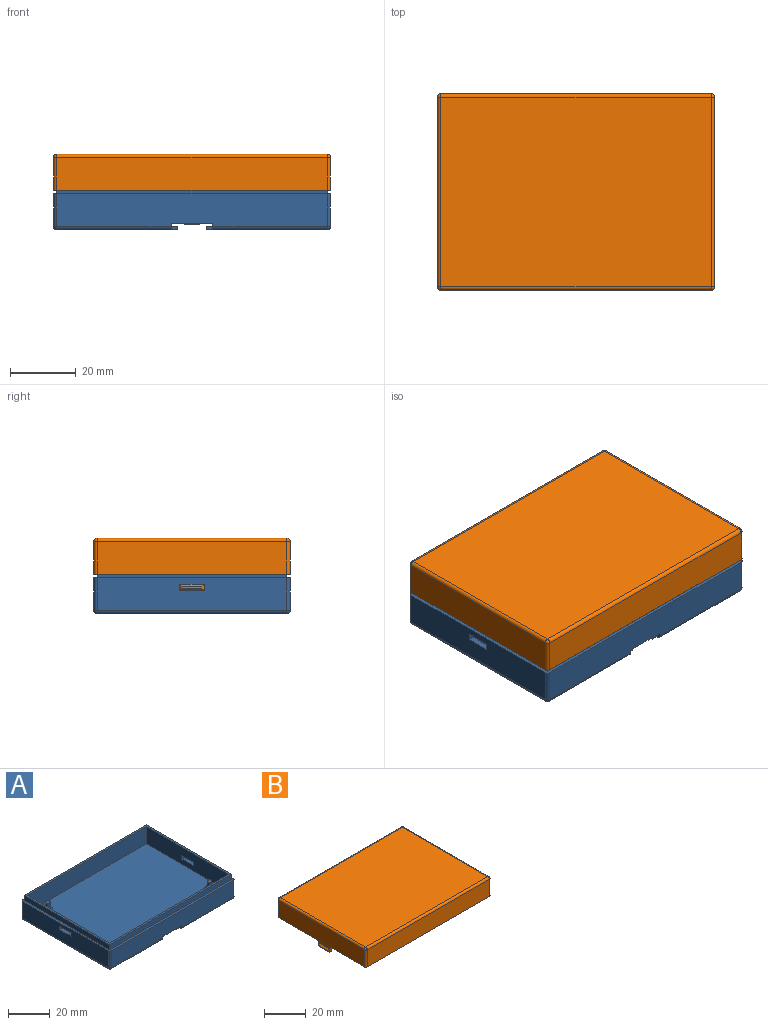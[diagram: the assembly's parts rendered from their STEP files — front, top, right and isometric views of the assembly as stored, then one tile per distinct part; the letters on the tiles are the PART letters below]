
ASSEMBLY  parts=2 mates=1
PART A: 106 faces, bbox 84.3x59.8x14 mm
  f0: plane 82.25x10mm, normal (0,-1,0), area 809.8mm2, adj f30,f32,f45,f69,f88,f90,f95,f97
  f1: plane 82.25x10mm, normal (0,1,0), area 809.8mm2, adj f30,f43,f55,f69,f84,f85,f91,f92
  f2: plane 57.75x10mm, normal (1,0,0), area 562.5mm2, adj f69,f80,f81,f82,f83,f91,f94,f97
  f3: plane 57.75x10mm, normal (-1,0,0), area 562.5mm2, adj f69,f76,f77,f78,f79,f85,f87,f88
  f4: plane 57.75x36.75mm, normal (0,0,-1), area 2104.3mm2, adj f6,f7,f8,f9,f44,f45,f46,f47
  f5: plane 57.75x36.75mm, normal (0,0,-1), area 2104.3mm2, adj f26,f27,f28,f29,f31,f32,f33,f34
  f6: plane 12.19x1mm, normal (-1,0,0), area 12.2mm2, adj f4,f10,f53,f56
  f7: plane 12.19x1mm, normal (-1,0,0), area 12.2mm2, adj f4,f11,f50,f52
  f8: plane 12.19x1mm, normal (-1,0,0), area 12.2mm2, adj f4,f12,f46,f49
  f9: plane 12.19x1mm, normal (-1,0,0), area 12.2mm2, adj f4,f13,f44,f47
  f10: plane 12.19x1.88mm, normal (0,0,1), area 22.9mm2, adj f6,f14,f53,f56
  f11: plane 12.19x1.88mm, normal (0,0,1), area 22.9mm2, adj f7,f15,f50,f52
  f12: plane 12.19x1.88mm, normal (0,0,1), area 22.9mm2, adj f8,f16,f46,f49
  f13: plane 12.19x1.88mm, normal (0,0,1), area 22.9mm2, adj f9,f17,f44,f47
  f14: plane 12.19x1mm, normal (-1,0,0), area 12.2mm2, adj f10,f30,f53,f56
  f15: plane 12.19x1mm, normal (-1,0,0), area 12.2mm2, adj f11,f30,f50,f52
  f16: plane 12.19x1mm, normal (-1,0,0), area 12.2mm2, adj f12,f30,f46,f49
  f17: plane 12.19x1mm, normal (-1,0,0), area 12.2mm2, adj f13,f30,f44,f47
  f18: plane 12.19x1mm, normal (1,0,0), area 12.2mm2, adj f22,f30,f39,f42
  f19: plane 12.19x1mm, normal (1,0,0), area 12.2mm2, adj f23,f30,f36,f40
  f20: plane 12.19x1mm, normal (1,0,0), area 12.2mm2, adj f24,f30,f33,f37
  f21: plane 12.19x1mm, normal (1,0,0), area 12.2mm2, adj f25,f30,f31,f34
  f22: plane 12.19x1.88mm, normal (0,0,1), area 22.9mm2, adj f18,f26,f39,f42
  f23: plane 12.19x1.88mm, normal (0,0,1), area 22.9mm2, adj f19,f27,f36,f40
  f24: plane 12.19x1.88mm, normal (0,0,1), area 22.9mm2, adj f20,f28,f33,f37
  f25: plane 12.19x1.88mm, normal (0,0,1), area 22.9mm2, adj f21,f29,f31,f34
  f26: plane 12.19x1mm, normal (1,0,0), area 12.2mm2, adj f5,f22,f39,f42
  f27: plane 12.19x1mm, normal (1,0,0), area 12.2mm2, adj f5,f23,f36,f40
  f28: plane 12.19x1mm, normal (1,0,0), area 12.2mm2, adj f5,f24,f33,f37
  f29: plane 12.19x1mm, normal (1,0,0), area 12.2mm2, adj f5,f25,f31,f34
  f30: plane 59.75x12.75mm, normal (0,0,-1), area 678.7mm2, adj f0,f1,f14,f15,f16,f17,f18,f19
  f31: plane 2x2mm, normal (0,-1,0), area 2.1mm2, adj f5,f21,f25,f29,f30,f32
  f32: plane 2x1.38mm, normal (1,0,0), area 2.5mm2, adj f0,f5,f30,f31,f90
  f33: plane 2x2mm, normal (0,-1,0), area 2.1mm2, adj f5,f20,f24,f28,f30,f35
  f34: plane 2x2mm, normal (0,1,0), area 2.1mm2, adj f5,f21,f25,f29,f30,f35
  f35: plane 2.75x2mm, normal (1,0,0), area 5.5mm2, adj f5,f30,f33,f34
  f36: plane 2x2mm, normal (0,-1,0), area 2.1mm2, adj f5,f19,f23,f27,f30,f38
  f37: plane 2x2mm, normal (0,1,0), area 2.1mm2, adj f5,f20,f24,f28,f30,f38
  f38: plane 2.75x2mm, normal (1,0,0), area 5.5mm2, adj f5,f30,f36,f37
  f39: plane 2x2mm, normal (0,-1,0), area 2.1mm2, adj f5,f18,f22,f26,f30,f41
  f40: plane 2x2mm, normal (0,1,0), area 2.1mm2, adj f5,f19,f23,f27,f30,f41
  f41: plane 2.75x2mm, normal (1,0,0), area 5.5mm2, adj f5,f30,f39,f40
  f42: plane 2x2mm, normal (0,1,0), area 2.1mm2, adj f5,f18,f22,f26,f30,f43
  f43: plane 2x1.38mm, normal (1,0,0), area 2.5mm2, adj f1,f5,f30,f42,f84
  f44: plane 2x2mm, normal (0,-1,0), area 2.1mm2, adj f4,f9,f13,f17,f30,f45
  f45: plane 2x1.38mm, normal (-1,0,0), area 2.5mm2, adj f0,f4,f30,f44,f95
  f46: plane 2x2mm, normal (0,-1,0), area 2.1mm2, adj f4,f8,f12,f16,f30,f48
  f47: plane 2x2mm, normal (0,1,0), area 2.1mm2, adj f4,f9,f13,f17,f30,f48
  f48: plane 2.75x2mm, normal (-1,0,0), area 5.5mm2, adj f4,f30,f46,f47
  f49: plane 2x2mm, normal (0,1,0), area 2.1mm2, adj f4,f8,f12,f16,f30,f51
  f50: plane 2x2mm, normal (0,-1,0), area 2.1mm2, adj f4,f7,f11,f15,f30,f51
  f51: plane 2.75x2mm, normal (-1,0,0), area 5.5mm2, adj f4,f30,f49,f50
  f52: plane 2x2mm, normal (0,1,0), area 2.1mm2, adj f4,f7,f11,f15,f30,f54
  f53: plane 2x2mm, normal (0,-1,0), area 2.1mm2, adj f4,f6,f10,f14,f30,f54
  f54: plane 2.75x2mm, normal (-1,0,0), area 5.5mm2, adj f4,f30,f52,f53
  f55: plane 2x1.38mm, normal (-1,0,0), area 2.5mm2, adj f1,f4,f30,f56,f92
  f56: plane 2x2mm, normal (0,1,0), area 2.1mm2, adj f4,f6,f10,f14,f30,f55
  f57: cylinder r=2.38mm len=4.75mm, axis (0,0,1), area 3.7mm2, adj f30,f58
  f58: plane 4.75x4.75mm, normal (0,0,-1), area 17.7mm2, adj f57
  f59: cylinder r=2.38mm len=4.75mm, axis (0,0,1), area 3.7mm2, adj f30,f60
  f60: plane 4.75x4.75mm, normal (0,0,-1), area 17.7mm2, adj f59
  f61: cylinder r=2.38mm len=4.75mm, axis (0,0,1), area 3.7mm2, adj f30,f62
  f62: plane 4.75x4.75mm, normal (0,0,-1), area 17.7mm2, adj f61
  f63: cylinder r=2.38mm len=4.75mm, axis (0,0,1), area 3.7mm2, adj f30,f64
  f64: plane 4.75x4.75mm, normal (0,0,-1), area 17.7mm2, adj f63
  f65: plane 57.75x3mm, normal (1,0,0), area 173.3mm2, adj f66,f68,f69,f75
  f66: plane 82.25x3mm, normal (0,-1,0), area 246.8mm2, adj f65,f67,f69,f75
  f67: plane 57.75x3mm, normal (-1,0,0), area 173.3mm2, adj f66,f68,f69,f75
  f68: plane 82.25x3mm, normal (0,1,0), area 246.8mm2, adj f65,f67,f69,f75
  f69: plane 84.25x59.75mm, normal (0,0,1), area 283.1mm2, adj f0,f1,f2,f3,f65,f66,f67,f68
  f70: plane 80.25x55.75mm, normal (0,0,1), area 4442.1mm2, adj f71,f72,f73,f74,f98,f102
  f71: plane 55.75x10mm, normal (-1,0,0), area 542.5mm2, adj f70,f72,f74,f75,f80,f81,f82,f83
  f72: plane 80.25x10mm, normal (0,-1,0), area 802.5mm2, adj f70,f71,f73,f75
  f73: plane 55.75x10mm, normal (1,0,0), area 542.5mm2, adj f70,f72,f74,f75,f76,f77,f78,f79
  f74: plane 80.25x10mm, normal (0,1,0), area 802.5mm2, adj f70,f71,f73,f75
  f75: plane 82.25x57.75mm, normal (0,0,1), area 276mm2, adj f65,f66,f67,f68,f71,f72,f73,f74
  f76: plane 7.5x2mm, normal (0,0,1), area 15mm2, adj f3,f73,f77,f79
  f77: plane 2x2mm, normal (0,1,0), area 4mm2, adj f3,f73,f76,f78
  f78: plane 7.5x2mm, normal (0,0,-1), area 15mm2, adj f3,f73,f77,f79
  f79: plane 2x2mm, normal (0,-1,0), area 4mm2, adj f3,f73,f76,f78
  f80: plane 2x2mm, normal (0,-1,0), area 4mm2, adj f2,f71,f81,f83
  f81: plane 7.5x2mm, normal (0,0,-1), area 15mm2, adj f2,f71,f80,f82
  f82: plane 2x2mm, normal (0,1,0), area 4mm2, adj f2,f71,f81,f83
  f83: plane 7.5x2mm, normal (0,0,1), area 15mm2, adj f2,f71,f80,f82
  f84: cylinder r=1mm len=34.75mm, axis (-1,0,0), area 54.6mm2, adj f1,f5,f43,f86
  f85: cylinder r=1mm len=10mm, axis (0,0,-1), area 15.7mm2, adj f1,f3,f69,f86
  f86: sphere r=1mm, area 1.6mm2, adj f84,f85,f87
  f87: cylinder r=1mm len=57.75mm, axis (0,-1,0), area 90.7mm2, adj f3,f5,f86,f89
  f88: cylinder r=1mm len=10mm, axis (0,0,1), area 15.7mm2, adj f0,f3,f69,f89
  f89: sphere r=1mm, area 1.6mm2, adj f87,f88,f90
  f90: cylinder r=1mm len=34.75mm, axis (1,0,0), area 54.6mm2, adj f0,f5,f32,f89
  f91: cylinder r=1mm len=10mm, axis (0,0,1), area 15.7mm2, adj f1,f2,f69,f93
  f92: cylinder r=1mm len=34.75mm, axis (-1,0,0), area 54.6mm2, adj f1,f4,f55,f93
  f93: sphere r=1mm, area 1.6mm2, adj f91,f92,f94
  f94: cylinder r=1mm len=57.75mm, axis (0,1,0), area 90.7mm2, adj f2,f4,f93,f96
  f95: cylinder r=1mm len=34.75mm, axis (1,0,0), area 54.6mm2, adj f0,f4,f45,f96
  f96: sphere r=1mm, area 1.6mm2, adj f94,f95,f97
  f97: cylinder r=1mm len=10mm, axis (0,0,-1), area 15.7mm2, adj f0,f2,f69,f96
  f98: cylinder r=2.25mm len=4.5mm, axis (0,0,-1), area 35.9mm2, adj f70,f99
  f99: plane 4.5x4.5mm, normal (0,0,1), area 11.9mm2, adj f98,f100
  f100: cylinder r=1.12mm len=4mm, axis (0,0,-1), area 28.3mm2, adj f99,f101
  f101: plane 2.25x2.25mm, normal (0,0,1), area 4mm2, adj f100
  f102: cylinder r=2.25mm len=4.5mm, axis (0,0,-1), area 35.9mm2, adj f70,f103
  f103: plane 4.5x4.5mm, normal (0,0,1), area 11.9mm2, adj f102,f104
  f104: cylinder r=1.12mm len=4mm, axis (0,0,-1), area 28.3mm2, adj f103,f105
  f105: plane 2.25x2.25mm, normal (0,0,1), area 4mm2, adj f104
PART B: 52 faces, bbox 84.3x59.8x16 mm
  f0: plane 80.25x55.75mm, normal (0,0,-1), area 4455.2mm2, adj f1,f2,f14,f15,f16,f17,f19,f21
  f1: plane 24.13x7mm, normal (-1,0,0), area 168.9mm2, adj f0,f13,f17,f42
  f2: plane 24.13x7mm, normal (1,0,0), area 168.9mm2, adj f0,f13,f15,f21
  f3: plane 82.25x10mm, normal (0,-1,0), area 822.5mm2, adj f8,f25,f31,f34
  f4: plane 57.75x10mm, normal (1,0,0), area 577.5mm2, adj f8,f28,f32,f34
  f5: plane 82.25x10mm, normal (0,1,0), area 822.5mm2, adj f8,f23,f27,f28
  f6: plane 57.75x10mm, normal (-1,0,0), area 577.5mm2, adj f8,f23,f25,f26
  f7: plane 82.25x57.75mm, normal (0,0,1), area 4749.9mm2, adj f26,f27,f31,f32
  f8: plane 84.25x59.75mm, normal (0,0,-1), area 283.1mm2, adj f3,f4,f5,f6,f9,f10,f11,f12
  f9: plane 82.25x2mm, normal (0,1,0), area 164.5mm2, adj f8,f10,f12,f13
  f10: plane 57.75x2mm, normal (1,0,0), area 115.5mm2, adj f8,f9,f11,f13
  f11: plane 82.25x2mm, normal (0,-1,0), area 164.5mm2, adj f8,f10,f12,f13
  f12: plane 57.75x2mm, normal (-1,0,0), area 115.5mm2, adj f8,f9,f11,f13
  f13: plane 82.25x57.75mm, normal (0,0,-1), area 276mm2, adj f1,f2,f9,f10,f11,f12,f14,f15
  f14: plane 24.13x7mm, normal (-1,0,0), area 168.9mm2, adj f0,f13,f15,f44
  f15: plane 80.25x7mm, normal (0,-1,0), area 561.8mm2, adj f0,f2,f13,f14
  f16: plane 24.13x7mm, normal (1,0,0), area 168.9mm2, adj f0,f13,f17,f19
  f17: plane 80.25x7mm, normal (0,1,0), area 561.8mm2, adj f0,f1,f13,f16
  f18: plane 7.5x5mm, normal (-1,0,0), area 37.5mm2, adj f13,f19,f21,f35
  f19: plane 14x1.45mm, normal (0,-1,0), area 17.9mm2, adj f0,f16,f18,f20,f22,f35,f40
  f20: plane 7.5x1.45mm, normal (0,0,-1), area 10.9mm2, adj f19,f21,f22,f38
  f21: plane 14x1.45mm, normal (0,1,0), area 17.9mm2, adj f0,f2,f18,f20,f22,f35,f37
  f22: plane 14x7.5mm, normal (1,0,0), area 105mm2, adj f0,f19,f20,f21
  f23: cylinder r=1mm len=10mm, axis (0,0,-1), area 15.7mm2, adj f5,f6,f8,f24
  f24: sphere r=1mm, area 1.6mm2, adj f23,f26,f27
  f25: cylinder r=1mm len=10mm, axis (0,0,1), area 15.7mm2, adj f3,f6,f8,f29
  f26: cylinder r=1mm len=57.75mm, axis (0,1,0), area 90.7mm2, adj f6,f7,f24,f29
  f27: cylinder r=1mm len=82.25mm, axis (1,0,0), area 129.2mm2, adj f5,f7,f24,f30
  f28: cylinder r=1mm len=10mm, axis (0,0,1), area 15.7mm2, adj f4,f5,f8,f30
  f29: sphere r=1mm, area 1.6mm2, adj f25,f26,f31
  f30: sphere r=1mm, area 1.6mm2, adj f27,f28,f32
  f31: cylinder r=1mm len=82.25mm, axis (-1,0,0), area 129.2mm2, adj f3,f7,f29,f33
  f32: cylinder r=1mm len=57.75mm, axis (0,-1,0), area 90.7mm2, adj f4,f7,f30,f33
  f33: sphere r=1mm, area 1.6mm2, adj f31,f32,f34
  f34: cylinder r=1mm len=10mm, axis (0,0,-1), area 15.7mm2, adj f3,f4,f8,f33
  f35: plane 7.5x0.2mm, normal (0,0,1), area 1.5mm2, adj f18,f19,f21,f39
  f36: plane 5.9x0.4mm, normal (-1,0,0), area 2.4mm2, adj f37,f38,f39,f40
  f37: plane 2x0.8mm, normal (-0.71,0.71,0), area 1.4mm2, adj f21,f36,f38,f39
  f38: plane 7.5x0.8mm, normal (-0.71,0,-0.71), area 7.6mm2, adj f20,f36,f37,f40
  f39: plane 7.5x0.8mm, normal (-0.71,0,0.71), area 7.6mm2, adj f35,f36,f37,f40
  f40: plane 2x0.8mm, normal (-0.71,-0.71,0), area 1.4mm2, adj f19,f36,f38,f39
  f41: plane 7.5x5mm, normal (1,0,0), area 37.5mm2, adj f13,f42,f44,f46
  f42: plane 14x1.45mm, normal (0,-1,0), area 17.9mm2, adj f0,f1,f41,f43,f45,f46,f51
  f43: plane 7.5x1.45mm, normal (0,0,-1), area 10.9mm2, adj f42,f44,f45,f49
  f44: plane 14x1.45mm, normal (0,1,0), area 17.9mm2, adj f0,f14,f41,f43,f45,f46,f48
  f45: plane 14x7.5mm, normal (-1,0,0), area 105mm2, adj f0,f42,f43,f44
  f46: plane 7.5x0.2mm, normal (0,0,1), area 1.5mm2, adj f41,f42,f44,f50
  f47: plane 5.9x0.4mm, normal (1,0,0), area 2.4mm2, adj f48,f49,f50,f51
  f48: plane 2x0.8mm, normal (0.71,0.71,0), area 1.4mm2, adj f44,f47,f49,f50
  f49: plane 7.5x0.8mm, normal (0.71,0,-0.71), area 7.6mm2, adj f43,f47,f48,f51
  f50: plane 7.5x0.8mm, normal (0.71,0,0.71), area 7.6mm2, adj f46,f47,f48,f51
  f51: plane 2x0.8mm, normal (0.71,-0.71,0), area 1.4mm2, adj f42,f47,f49,f50
PLACE A t=(-2.05,0.86,-3.93)mm fixed
PLACE B t=(-2.05,0.86,8.07)mm
MATE slider A.f97 <-> B.f34  axis (0,0,1) through (39.08,-28.01,10.07)mm
